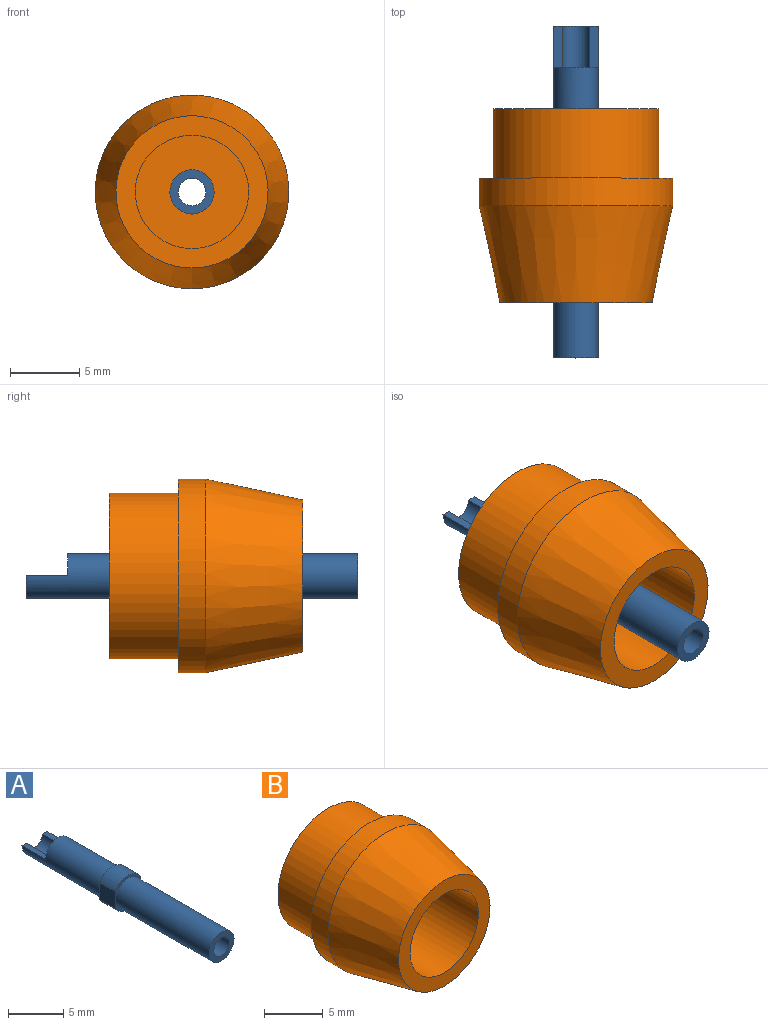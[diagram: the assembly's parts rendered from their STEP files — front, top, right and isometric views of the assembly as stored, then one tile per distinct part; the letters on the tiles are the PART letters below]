
ASSEMBLY  parts=2 mates=1
PART A: 14 faces, bbox 3.3x24x3.8 mm
  f0: cylinder r=1mm len=24mm, axis (0,-1,0), area 141.4mm2, adj f1,f8,f11,f12,f13
  f1: plane 3.2x1.6mm, normal (0,1,0), area 2.5mm2, adj f0,f2,f12,f13
  f2: cylinder r=1.6mm len=10mm, axis (0,-1,0), area 85.5mm2, adj f1,f3,f11,f12,f13
  f3: plane 3.8x3.3mm, normal (0,1,0), area 2.7mm2, adj f2,f4,f5,f9,f10
  f4: cylinder r=1.9mm len=3.3mm, axis (0,-1,0), area 8mm2, adj f3,f6,f9,f10
  f5: cylinder r=1.9mm len=3.3mm, axis (0,-1,0), area 8mm2, adj f3,f6,f9,f10
  f6: plane 3.8x3.3mm, normal (0,-1,0), area 2.7mm2, adj f4,f5,f7,f9,f10
  f7: cylinder r=1.6mm len=12mm, axis (0,-1,0), area 120.6mm2, adj f6,f8
  f8: plane 3.2x3.2mm, normal (0,-1,0), area 4.9mm2, adj f0,f7
  f9: plane 2x1.88mm, normal (1,0,0), area 3.8mm2, adj f3,f4,f5,f6
  f10: plane 2x1.88mm, normal (-1,0,0), area 3.8mm2, adj f3,f4,f5,f6
  f11: plane 3.2x1.6mm, normal (0,1,0), area 2.5mm2, adj f0,f2,f12,f13
  f12: plane 3x0.6mm, normal (0,0,1), area 1.8mm2, adj f0,f1,f2,f11
  f13: plane 3x0.6mm, normal (0,0,1), area 1.8mm2, adj f0,f1,f2,f11
PART B: 16 faces, bbox 14x14x14 mm
  f0: cylinder r=1.6mm len=3.2mm, axis (0,-1,0), area 10.1mm2, adj f1,f15
  f1: plane 8.2x8.2mm, normal (0,-1,0), area 44.8mm2, adj f0,f10
  f2: plane 8x8mm, normal (0,1,0), area 39.6mm2, adj f3,f11,f12,f13,f14
  f3: cylinder r=4mm len=8mm, axis (0,-1,0), area 100.5mm2, adj f2,f4
  f4: plane 12x12mm, normal (0,1,0), area 62.8mm2, adj f3,f5
  f5: cylinder r=6mm len=12mm, axis (0,-1,0), area 188.5mm2, adj f4,f6
  f6: plane 14x14mm, normal (0,1,0), area 40.8mm2, adj f5,f7
  f7: cylinder r=7mm len=14mm, axis (0,-1,0), area 88mm2, adj f6,f8
  f8: cone r=7mm half-angle=12.1deg, axis (0,1,0), area 281.1mm2, adj f7,f9
  f9: plane 11x11mm, normal (0,-1,0), area 42.2mm2, adj f8,f10
  f10: cylinder r=4.1mm len=8.2mm, axis (0,-1,0), area 180.3mm2, adj f1,f9
  f11: plane 2x1.88mm, normal (-1,0,0), area 3.8mm2, adj f2,f12,f14,f15
  f12: cylinder r=1.9mm len=3.3mm, axis (0,1,0), area 8mm2, adj f2,f11,f13,f15
  f13: plane 2x1.88mm, normal (1,0,0), area 3.8mm2, adj f2,f12,f14,f15
  f14: cylinder r=1.9mm len=3.3mm, axis (0,1,0), area 8mm2, adj f2,f11,f13,f15
  f15: plane 3.8x3.3mm, normal (0,1,0), area 2.7mm2, adj f0,f11,f12,f13,f14
PLACE A t=(0,-4,0)mm
PLACE B at identity
MATE fastened A.f0 <-> B.f0  axis (0,-1,0) through (0,8,0)mm
